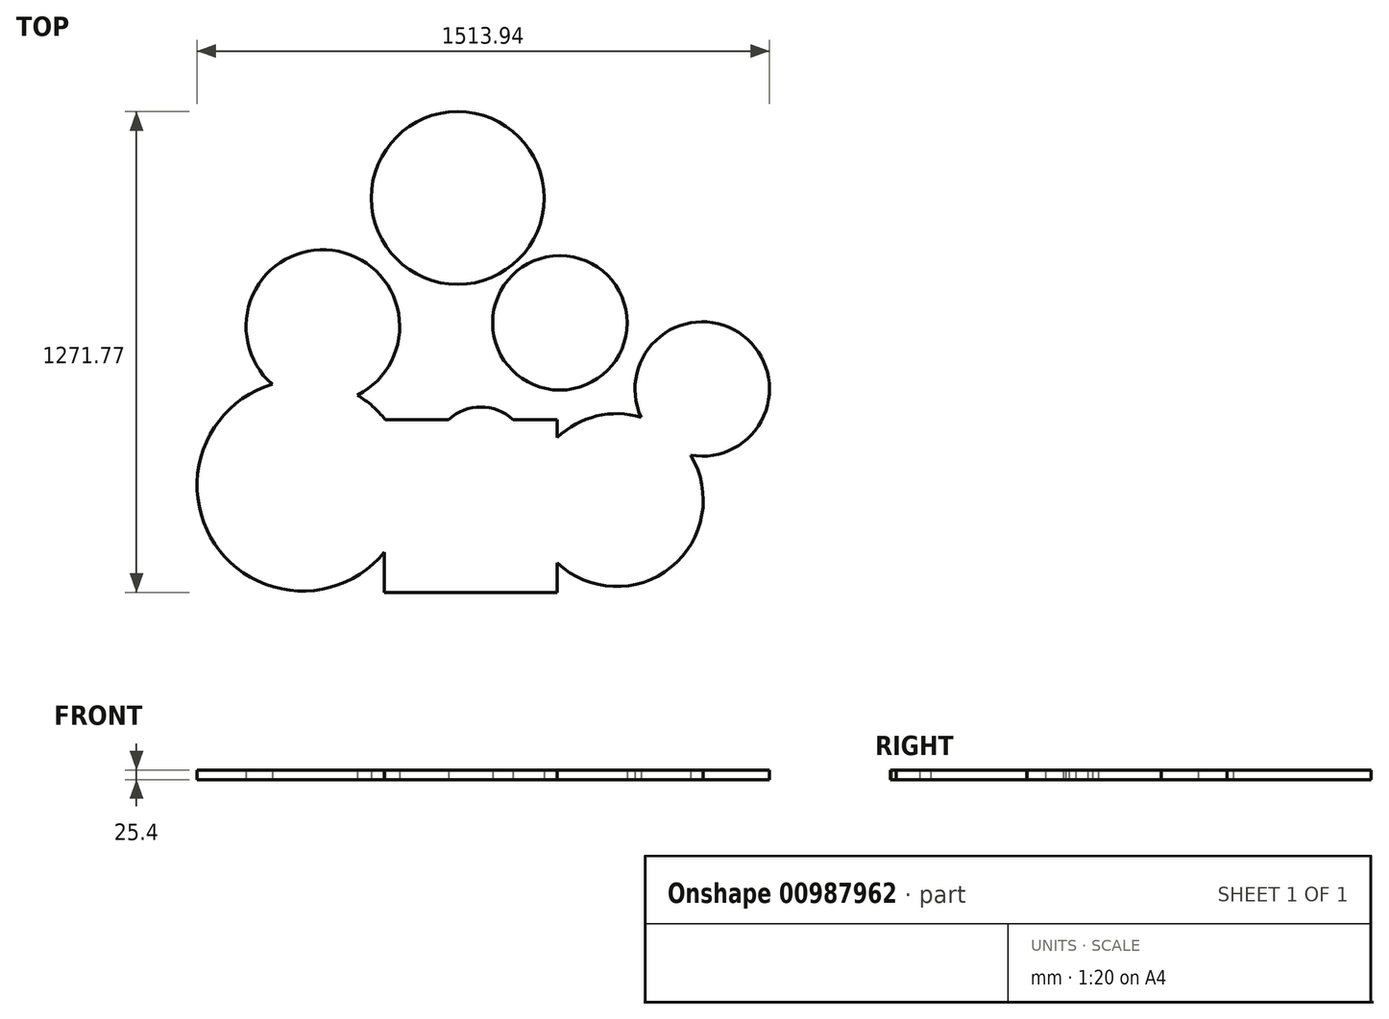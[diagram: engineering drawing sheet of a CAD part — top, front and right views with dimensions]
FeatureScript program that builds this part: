
annotation { "Feature Type Name" : "Feature", "Feature Type Description" : "" }
export const myFeature = defineFeature(function(context is Context, id is Id, definition is map)
    precondition{}
    {
        {
            var Q0;
            Q0=qCreatedBy(makeId("Top.planeOp"),FACE);
            var sketch = newSketch(context, id + "F0", { "sketchPlane" : qUnion([Q0])});
            skLineSegment(sketch, "E0.bottom", {"start": v(0, 0) * mm, "end": v(457.2, 0) * mm});
            skLineSegment(sketch, "E0.top", {"start": v(0, 457.2) * mm, "end": v(457.2, 457.2) * mm});
            skLineSegment(sketch, "E0.left", {"start": v(0, 0) * mm, "end": v(0, 457.2) * mm});
            skLineSegment(sketch, "E0.right", {"start": v(457.2, 0) * mm, "end": v(457.2, 457.2) * mm});
            skCircle(sketch, "E1", {"center": v(463.73, 712.8) * mm, "radius": 177.8 * mm});
            skCircle(sketch, "E2", {"center": v(-163.03, 703.09) * mm, "radius": 203.2 * mm});
            skCircle(sketch, "E3", {"center": v(-216.47, 282.82) * mm, "radius": 279.4 * mm});
            skCircle(sketch, "E4", {"center": v(254.81, 362.98) * mm, "radius": 127 * mm});
            skCircle(sketch, "E5", {"center": v(840.27, 537.9) * mm, "radius": 177.8 * mm});
            skCircle(sketch, "E6", {"center": v(614.35, 243.95) * mm, "radius": 228.6 * mm});
            skCircle(sketch, "E7", {"center": v(193.53, 1043.17) * mm, "radius": 228.6 * mm});
            skSolve(sketch);
        }
        {
            var Q0;
            Q0 = qSketchRegion(id + "F0", true);
            extrude(context, id + "F1", {"entities" : qUnion([Q0]), "depth" : 25.4 * mm, "offsetDistance" : 25.4 * mm});
        }
    });
